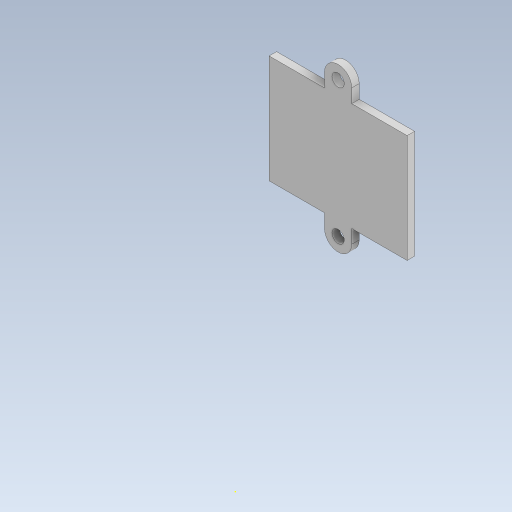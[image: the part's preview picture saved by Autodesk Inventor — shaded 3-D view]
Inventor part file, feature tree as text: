
AUTODESK INVENTOR PART (.ipt)
format: ipt  version: 2024.2 (Build 282272000, 272)  size: 368,640 bytes
history: native  units: mm
features: extrude x11, sketch x8, fillet x3, projected_geometry x3, plane x2, other x2, pattern_linear x1, chamfer x1
ambient origin geometry x8: Origin, YZ Plane, XZ Plane, XY Plane, X Axis, Y Axis, Z Axis, Center Point
bodies: Solid1 (feature_tree)
feature tree (31):
  sketch  "Sketch1"  dims[d0=20.0mm d1=40.5mm]
  extrude  "Extrusion1"  Depth=40.5mm
  extrude  "Extrusion3"  Depth=3.0mm
  plane  "Work Plane1"
  pattern_linear  "Rectangular Pattern1"  Count1=6 Spacing1=0.0mm
  sketch  "Sketch4"  dims[d2=3.0mm d3=3.0mm d4=60.0mm d5=0.0mm]
  extrude  "Extrusion5"  TaperAngle=45.0deg  [1 undecoded]
  sketch  "Sketch6"  dims[d15=3.0mm d16=0.0mm d17=30.0mm d19=28.5mm]
  extrude  "Extrusion6"  Depth=30.0mm
  extrude  "Extrusion7"  Depth=5.3mm
  extrude  "Extrusion8"  Depth=2.5mm
  extrude  "Extrusion9"  Depth=54.75mm
  fillet  "Fillet1"  Radius=39.8mm
  plane  "Work Plane2"
  sketch  "Sketch9"  dims[d31=118.75mm d32=54.75mm d34=39.8mm]
  extrude  "Extrusion10"  Depth=90.0mm TaperAngle=0.0deg
  extrude  "Extrusion11"  Depth=2.5mm TaperAngle=0.0deg
  extrude  "Extrusion12"  Depth=90.0mm TaperAngle=0.0deg
  fillet  "Fillet2"  Radius=10.0mm
  fillet  "Fillet3"  Radius=10.0mm
  chamfer  "Chamfer2"  Distance=3.0mm
  extrude  "Extrusion13"  Depth=2.0mm
  sketch  "Sketch5"  dims[d13=45.0deg d14=45.0deg]
  projected_geometry  "Projected Loop4"
  projected_geometry  "Projected Loop5"
  projected_geometry  "Projected Loop6"
  other  "electronics box"
  sketch  "Sketch7"  dims[d26=5.3mm d27=5.3mm]
  sketch  "Sketch8"  dims[d28=0.0mm d29=0.0mm d30=2.5mm]
  other  "canholder"
  sketch  "Sketch10"  dims[d35=38.45mm d36=90.0mm d37=0.0mm d38=2.5mm d39=0.0mm d40=90.0mm d41=0.0mm d42=10.0mm d43=10.0mm d44=0.0mm d45=3.0mm d46=50.0mm d47=28.0mm d48=0.5mm d49=10.0mm d50=5.0mm d51=3.3mm d52=2.0mm d53=3.5mm d54=0.0mm d55=3.5mm d56=37.0mm d57=2.0mm d58=0.0mm d59=27.5mm d60=5.0mm d61=10.0mm d62=2.0mm d63=0.0mm d64=2.5mm d65=3.0mm d66=2.5mm d67=2.0mm d68=45.0deg d70=5.58mm d71=10.0mm d72=10.0mm d73=2.0mm d74=0.0mm]
note: 1 required parameter value undecoded (feature->parameter linkage not recoverable at this tier; creation-order binding heuristic only, values carry confidence <= 0.55)
